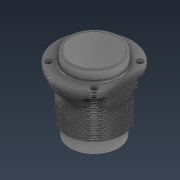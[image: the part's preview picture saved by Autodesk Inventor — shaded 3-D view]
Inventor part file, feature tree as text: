
AUTODESK INVENTOR PART (.ipt)
format: ipt  version: 2022 (Build 260153000, 153)  size: 2,409,472 bytes
history: native  units: mm
features: sketch x17, extrude x15, plane x12, fillet x5, hole x2, pattern_linear x2
ambient origin geometry x8: Origin, YZ Plane, XZ Plane, XY Plane, X Axis, Y Axis, Z Axis, Center Point
bodies: Solid1 (feature_tree)
feature tree (53):
  extrude  "Extrusion1"  Depth=90.0mm
  extrude  "Extrusion2"  Depth=98.0mm
  extrude  "Extrusion3"  Depth=94.0mm
  plane  "Work Plane1"
  extrude  "Extrusion4"  [1 undecoded]
  plane  "Work Plane2"
  extrude  "Extrusion5"  Depth=1.0mm TaperAngle=0.0deg
  plane  "Work Plane3"
  extrude  "Extrusion6"  Depth=139.0mm
  plane  "Work Plane4"
  extrude  "Extrusion7"  Depth=3.0mm
  plane  "Work Plane5"
  extrude  "Extrusion8"  Depth=1.0mm TaperAngle=0.0deg
  plane  "Work Plane6"
  extrude  "Extrusion9"  Depth=135.0mm
  plane  "Work Plane7"
  extrude  "Extrusion10"  Depth=3.0mm
  plane  "Work Plane8"
  extrude  "Extrusion11"  Depth=1.0mm TaperAngle=0.0deg
  plane  "Work Plane9"
  extrude  "Extrusion12"  Depth=128.0mm
  plane  "Work Plane10"
  extrude  "Extrusion13"  Depth=3.0mm
  plane  "Work Plane11"
  extrude  "Extrusion14"  Depth=1.0mm TaperAngle=0.0deg
  sketch  "Sketch15"  dims[d38=3.0mm d39=120.0mm]
  hole  "Hole1"  [1 undecoded]
  pattern_linear  "Rectangular Pattern1"  Spacing1=114.0mm  [1 undecoded]
  hole  "Hole2"  [1 undecoded]
  fillet  "Fillet1"  Radius=3.0mm
  fillet  "Fillet2"  Radius=110.0mm
  pattern_linear  "Rectangular Pattern2"  Spacing1=1.0mm  [1 undecoded]
  plane  "Work Plane12"
  extrude  "Extrusion15"  Depth=3.0mm
  fillet  "Fillet3"  Radius=106.0mm
  fillet  "Fillet4"  Radius=1.0mm
  fillet  "Fillet5"  Radius=121.5mm
  sketch  "Sketch1"  dims[d0=85.5mm d1=90.0mm]
  sketch  "Sketch2"  dims[d2=24.0mm d3=0.0mm d4=98.0mm]
  sketch  "Sketch3"  dims[d5=97.5mm d6=0.0mm d7=94.0mm]
  sketch  "Sketch4"  dims[d8=15.0mm d9=0.0mm d10=-3.0mm]
  sketch  "Sketch5"  dims[d11=140.0mm d12=1.0mm d13=0.0mm]
  sketch  "Sketch6"  dims[d14=3.0mm d15=139.0mm]
  sketch  "Sketch7"  dims[d16=1.0mm d17=0.0mm d18=3.0mm]
  sketch  "Sketch8"  dims[d19=137.0mm d20=1.0mm d21=0.0mm]
  sketch  "Sketch9"  dims[d22=3.0mm d23=135.0mm]
  sketch  "Sketch10"  dims[d24=1.0mm d25=0.0mm d26=3.0mm]
  sketch  "Sketch11"  dims[d27=132.0mm d28=1.0mm d29=0.0mm]
  sketch  "Sketch12"  dims[d30=3.0mm d31=128.0mm]
  sketch  "Sketch13"  dims[d32=1.0mm d33=0.0mm d34=3.0mm]
  sketch  "Sketch14"  dims[d35=124.0mm d36=1.0mm d37=0.0mm]
  sketch  "Sketch16"  dims[d40=1.0mm d41=0.0mm]
  sketch  "Sketch17"  dims[d42=3.0mm d43=114.0mm d44=1.0mm d45=0.0mm d46=3.0mm d47=110.0mm d48=1.0mm d49=0.0mm d50=3.0mm d51=106.0mm d52=1.0mm d53=0.0mm d54=121.5mm d55=45.0deg d56=40.0mm d58=360.0deg d60=11.5mm d61=6.0mm d62=4.0mm d63=2.0mm d64=90.0deg d65=12.4mm d66=20.594885mm d67=20.0mm d68=6.0mm d69=4.0mm d70=2.0mm d71=90.0deg d72=8.0mm d73=20.594885mm d74=10.0mm d75=140.0mm d77=-4.0mm d78=10.0mm d79=140.0mm d81=4.0mm d82=-80.0mm d83=16.0mm d84=1.0mm d85=0.0mm d86=8.0mm d87=1.5mm d88=0.5mm]
note: 5 required parameter values undecoded (feature->parameter linkage not recoverable at this tier; creation-order binding heuristic only, values carry confidence <= 0.55)
